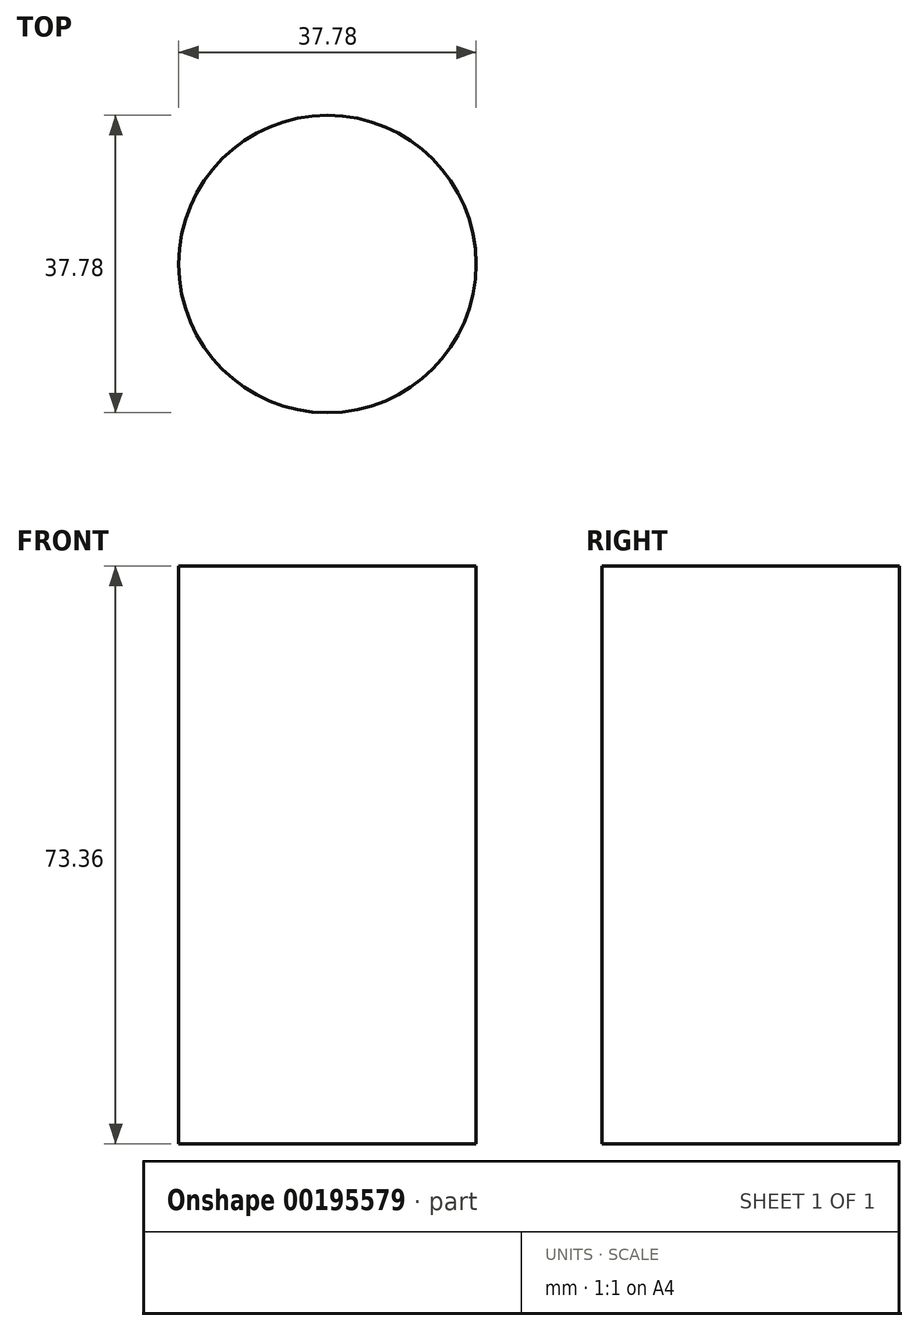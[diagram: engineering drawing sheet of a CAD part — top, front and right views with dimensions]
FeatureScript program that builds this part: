
annotation { "Feature Type Name" : "Feature", "Feature Type Description" : "" }
export const myFeature = defineFeature(function(context is Context, id is Id, definition is map)
    precondition{}
    {
        {
            var Q0;
            Q0=qCreatedBy(makeId("Front.planeOp"),FACE);
            var sketch = newSketch(context, id + "F0", { "sketchPlane" : qUnion([Q0])});
            skLineSegment(sketch, "E0", {"start": v(0, 0) * mm, "end": v(0, 73.36) * mm});
            skLineSegment(sketch, "E1", {"start": v(0, 73.36) * mm, "end": v(-18.9, 73.36) * mm});
            skLineSegment(sketch, "E2", {"start": v(-18.9, 73.36) * mm, "end": v(-18.9, 0) * mm});
            skLineSegment(sketch, "E3", {"start": v(-18.9, 0) * mm, "end": v(0, 0) * mm});
            skSolve(sketch);
        }
        {
            var Q0;
            Q0=makeQuery(id+"F0.imprint","IMPRINT",FACE,{"disambiguationData":[TD([[makeQuery(id+"F0.imprint","IMPRINT",EDGE,{"derivedFrom":sQuery(id+"F0.wireOp",EDGE,"E0")}),1.0]])]});
            var Q1;
            Q1=sQuery(id+"F0.wireOp",EDGE,"E0");
            revolve(context, id + "F1", {"entities" : qUnion([Q0]), "axis" : qUnion([Q1]), "revolveType" : RevolveType.FULL});
        }
    });
